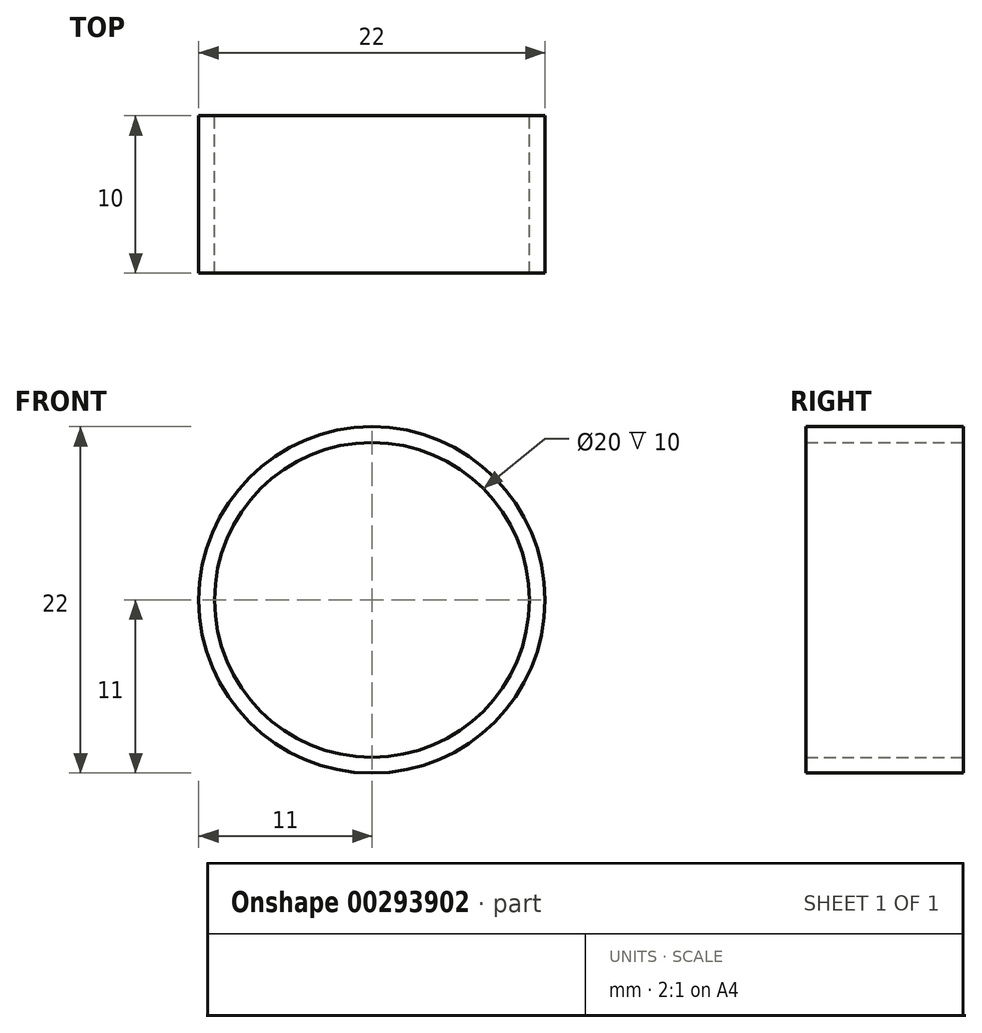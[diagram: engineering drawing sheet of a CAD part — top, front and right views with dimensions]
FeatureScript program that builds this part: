
annotation { "Feature Type Name" : "Feature", "Feature Type Description" : "" }
export const myFeature = defineFeature(function(context is Context, id is Id, definition is map)
    precondition{}
    {
        {
            var Q0;
            Q0=qCreatedBy(makeId("Front.planeOp"),FACE);
            var sketch = newSketch(context, id + "F0", { "sketchPlane" : qUnion([Q0])});
            skCircle(sketch, "E0", {"center": v(0, 0) * mm, "radius": 10 * mm});
            skCircle(sketch, "E1", {"center": v(0, 0) * mm, "radius": 11 * mm});
            skSolve(sketch);
        }
        {
            var Q0;
            Q0=makeQuery(id+"F0.imprint","IMPRINT",FACE,{"disambiguationData":[TD([[makeQuery(id+"F0.imprint","IMPRINT",EDGE,{"derivedFrom":sQuery(id+"F0.wireOp",EDGE,"E0")}),-1.0]])]});
            extrude(context, id + "F1", {"entities" : qUnion([Q0]), "depth" : 10 * mm});
        }
    });
